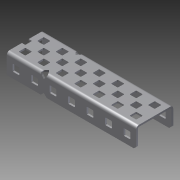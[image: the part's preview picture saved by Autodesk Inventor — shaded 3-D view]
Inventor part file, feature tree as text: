
AUTODESK INVENTOR PART (.ipt)
format: ipt  version: 2014 SP1 (Build 180222100, 222)  size: 712,192 bytes
history: native  units: in
note: dims shown in document units (in); Inventor stores cm internally (conversion verified against a paired STEP export)
features: other x1, imported_body x1, extrude x1, sketch x1
ambient origin geometry x8: Origin, YZ Plane, XZ Plane, XY Plane, X Axis, Y Axis, Z Axis, Center Point
bodies: Body1 (feature_tree)
feature tree (4):
  parser-record x1  (decoder bookkeeping rows leaked as tree rows — omitted from the tree; the rows remain in map.json)
  imported_body  "Base1"
  extrude  "Extrusion1"  Depth=1.0in TaperAngle=0.0deg
  sketch  "Sketch2"  dims[d0=1.5in d1=1.0in d2=0.0in]
